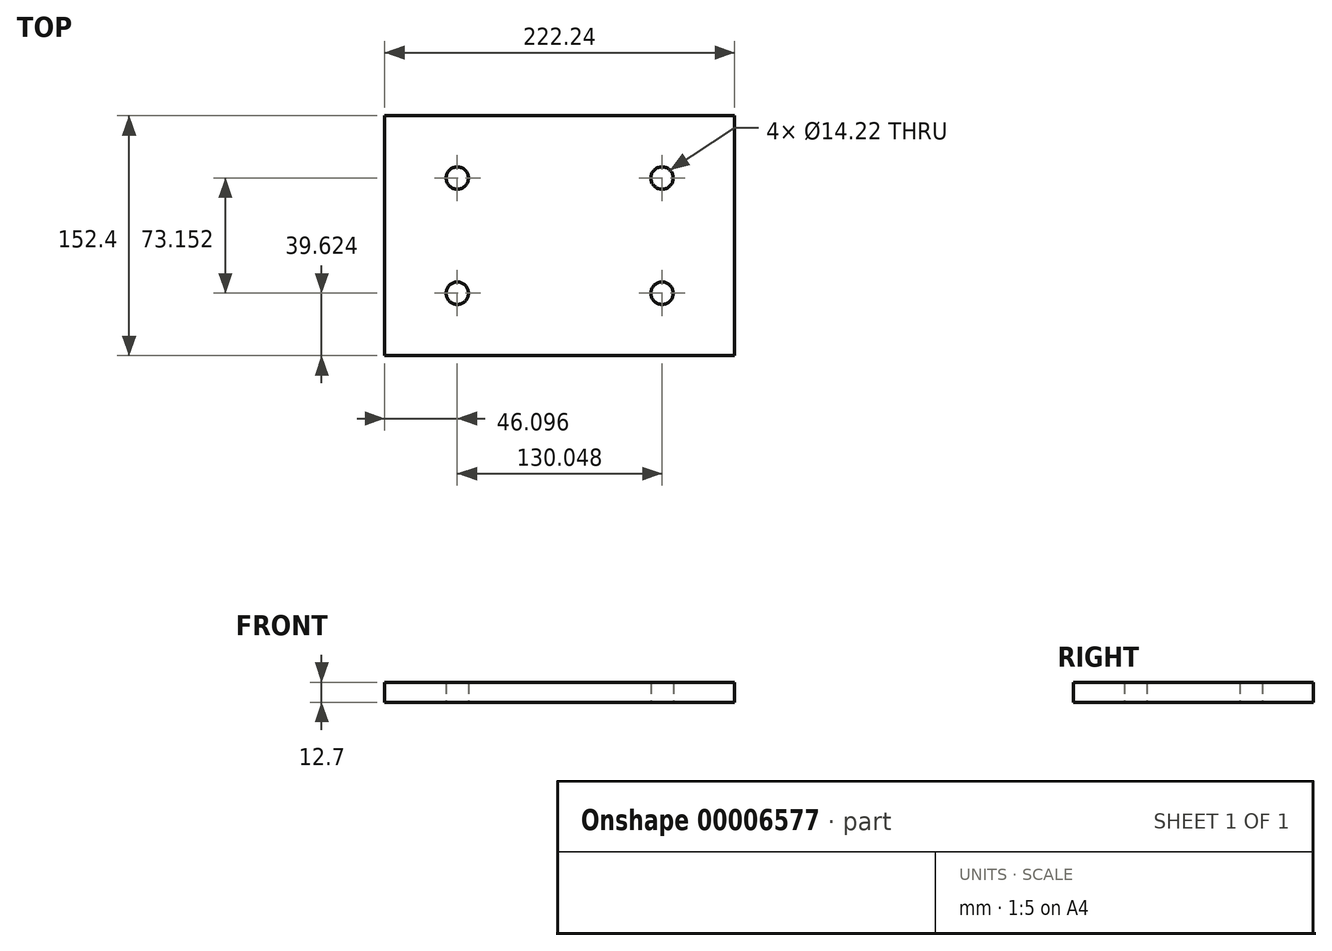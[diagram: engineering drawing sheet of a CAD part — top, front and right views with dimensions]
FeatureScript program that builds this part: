
annotation { "Feature Type Name" : "Feature", "Feature Type Description" : "" }
export const myFeature = defineFeature(function(context is Context, id is Id, definition is map)
    precondition{}
    {
        {
            var Q0;
            Q0=qCreatedBy(makeId("Top.planeOp"),FACE);
            var sketch = newSketch(context, id + "F0", { "sketchPlane" : qUnion([Q0])});
            skLineSegment(sketch, "E0.rect.bottom", {"start": v(-111.13, 76.2) * mm, "end": v(111.13, 76.2) * mm});
            skLineSegment(sketch, "E0.rect.top", {"start": v(-111.13, -76.2) * mm, "end": v(111.13, -76.2) * mm});
            skLineSegment(sketch, "E0.rect.left", {"start": v(-111.13, 76.2) * mm, "end": v(-111.13, -76.2) * mm});
            skLineSegment(sketch, "E0.rect.right", {"start": v(111.13, 76.2) * mm, "end": v(111.13, -76.2) * mm});
            skPoint(sketch, "E0.rect.middle", {"position": v(0, 0) * mm});
            skLineSegment(sketch, "E1.bottom", {"start": v(-111.13, 76.2) * mm, "end": v(0, 76.2) * mm, "construction": true});
            skLineSegment(sketch, "E1.top", {"start": v(-111.13, 0) * mm, "end": v(0, 0) * mm, "construction": true});
            skLineSegment(sketch, "E1.left", {"start": v(-111.13, 76.2) * mm, "end": v(-111.13, 0) * mm, "construction": true});
            skLineSegment(sketch, "E1.right", {"start": v(0, 76.2) * mm, "end": v(0, 0) * mm, "construction": true});
            skLineSegment(sketch, "E2.0", {"start": v(-65.02, 76.2) * mm, "end": v(-65.02, 0) * mm, "construction": true});
            skLineSegment(sketch, "E3.0", {"start": v(-111.13, 36.58) * mm, "end": v(0, 36.58) * mm, "construction": true});
            skCircle(sketch, "E4", {"center": v(-65.02, 36.58) * mm, "radius": 7.11 * mm});
            skCircle(sketch, "E5.0.MirrorC", {"center": v(65.02, 36.58) * mm, "radius": 7.11 * mm});
            skCircle(sketch, "E6.0.MirrorC", {"center": v(-65.02, -36.58) * mm, "radius": 7.11 * mm});
            skCircle(sketch, "E7.0.MirrorC", {"center": v(65.02, -36.58) * mm, "radius": 7.11 * mm});
            skSolve(sketch);
        }
        {
            var Q0;
            Q0=makeQuery(id+"F0.imprint","IMPRINT",FACE,{"disambiguationData":[TD([[makeQuery(id+"F0.imprint","IMPRINT",EDGE,{"derivedFrom":sQuery(id+"F0.wireOp",EDGE,"E0.rect.bottom")}),-1.0]])]});
            extrude(context, id + "F1", {"entities" : qUnion([Q0]), "depth" : 12.7 * mm});
        }
    });
